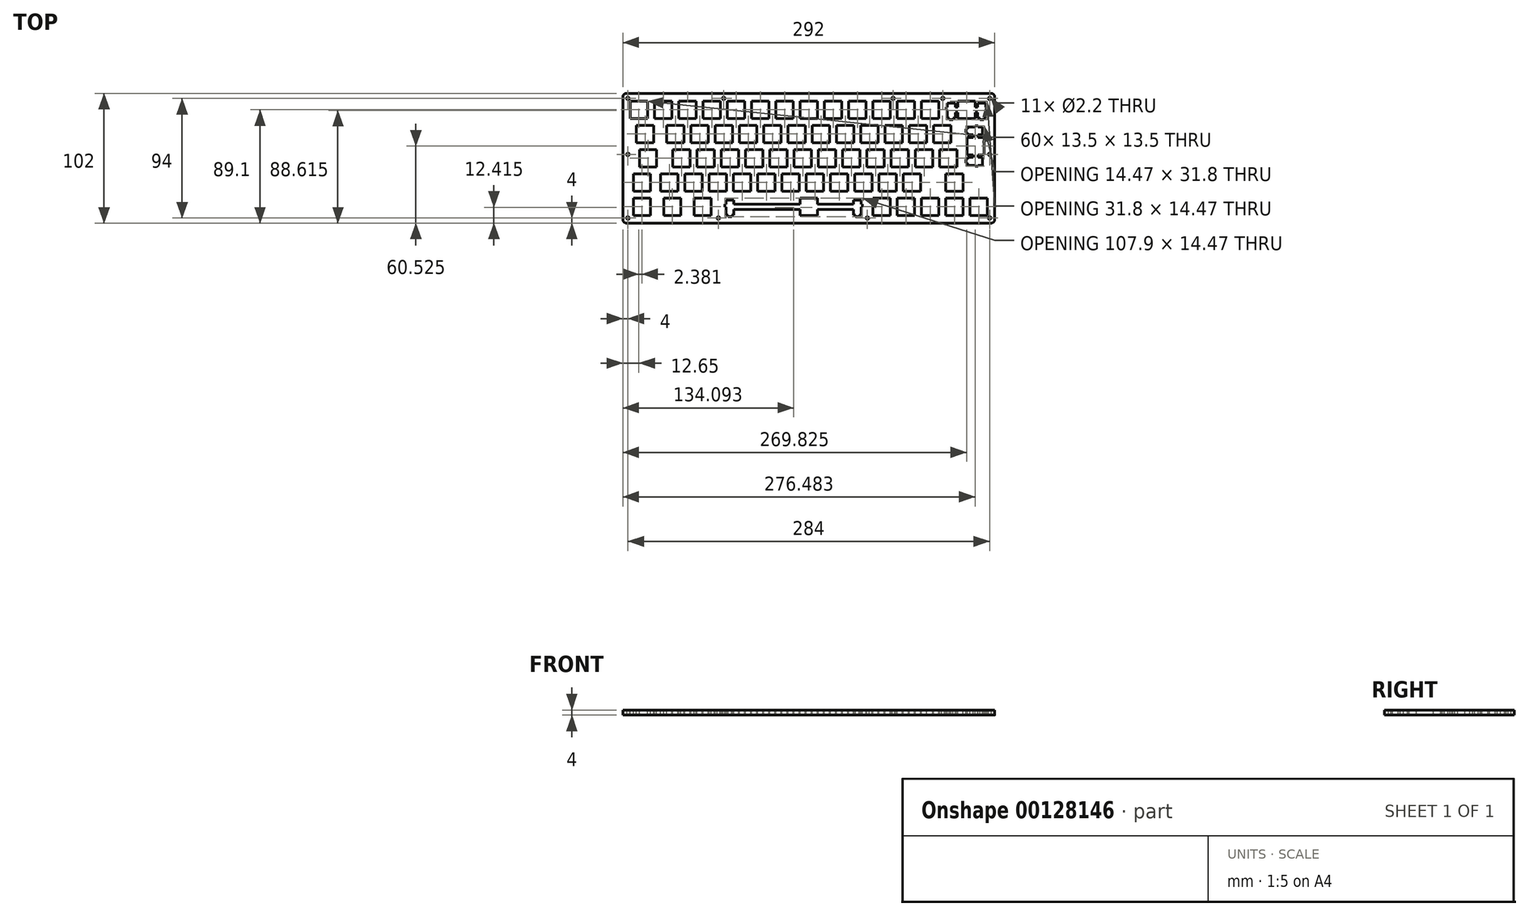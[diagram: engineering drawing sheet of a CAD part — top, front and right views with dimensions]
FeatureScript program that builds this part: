
annotation { "Feature Type Name" : "Feature", "Feature Type Description" : "" }
export const myFeature = defineFeature(function(context is Context, id is Id, definition is map)
    precondition{}
    {
        {
            var Q0;
            Q0=qCreatedBy(makeId("Top.planeOp"),FACE);
            var sketch = newSketch(context, id + "F0", { "sketchPlane" : qUnion([Q0])});
            skLineSegment(sketch, "E0.bottom", {"start": v(-143, 51) * mm, "end": v(143, 51) * mm});
            skLineSegment(sketch, "E0.top", {"start": v(-143, -51) * mm, "end": v(143, -51) * mm});
            skLineSegment(sketch, "E0.left", {"start": v(-146, 48) * mm, "end": v(-146, -48) * mm});
            skLineSegment(sketch, "E0.right", {"start": v(146, 48) * mm, "end": v(146, -48) * mm});
            skPoint(sketch, "E0.middle", {"position": v(0, 0) * mm});
            skPoint(sketch, "E1.visualSharp", {"position": v(-146, 51) * mm});
            skArc(sketch, "E1.filletArc", {"start": v(-143, 51) * mm, "mid": v(-145.12, 50.12) * mm, "end": v(-146, 48) * mm});
            skPoint(sketch, "E2.visualSharp", {"position": v(-146, -51) * mm});
            skArc(sketch, "E2.filletArc", {"start": v(-146, -48) * mm, "mid": v(-145.12, -50.12) * mm, "end": v(-143, -51) * mm});
            skPoint(sketch, "E3.visualSharp", {"position": v(146, 51) * mm});
            skArc(sketch, "E3.filletArc", {"start": v(146, 48) * mm, "mid": v(145.12, 50.12) * mm, "end": v(143, 51) * mm});
            skPoint(sketch, "E4.visualSharp", {"position": v(146, -51) * mm});
            skArc(sketch, "E4.filletArc", {"start": v(143, -51) * mm, "mid": v(145.12, -50.12) * mm, "end": v(146, -48) * mm});
            skCircle(sketch, "E5", {"center": v(-142, 47) * mm, "radius": 1.1 * mm});
            skCircle(sketch, "E6", {"center": v(-66.83, 47) * mm, "radius": 1.1 * mm});
            skCircle(sketch, "E7", {"center": v(66.17, 47) * mm, "radius": 1.1 * mm});
            skCircle(sketch, "E8", {"center": v(105.17, 47) * mm, "radius": 1.1 * mm});
            skCircle(sketch, "E9", {"center": v(142, 47) * mm, "radius": 1.1 * mm});
            skCircle(sketch, "E10", {"center": v(-142, -47) * mm, "radius": 1.1 * mm});
            skCircle(sketch, "E11", {"center": v(142, -47) * mm, "radius": 1.1 * mm});
            skCircle(sketch, "E12", {"center": v(-71, -47) * mm, "radius": 1.1 * mm});
            skCircle(sketch, "E13", {"center": v(46, -47) * mm, "radius": 1.1 * mm});
            skCircle(sketch, "E14", {"center": v(-142, 3) * mm, "radius": 1.1 * mm});
            skCircle(sketch, "E15", {"center": v(142, 3) * mm, "radius": 1.1 * mm});
            skSolve(sketch);
        }
        {
            var Q0;
            Q0=qSketchRegion(id+"F0",true);
            extrude(context, id + "F1", {"entities" : qUnion([Q0]), "depth" : 4 * mm});
        }
        {
            var Q0;
            Q0=makeQuery(id+"F1.opExtrude","CAP_FACE",FACE,{"disambiguationData":[OSD([sQuery(id+"F0.wireOp",EDGE,"E0.bottom"),sQuery(id+"F0.wireOp",EDGE,"E0.top"),sQuery(id+"F0.wireOp",EDGE,"E0.left"),sQuery(id+"F0.wireOp",EDGE,"E0.right"),sQuery(id+"F0.wireOp",EDGE,"E1.filletArc"),sQuery(id+"F0.wireOp",EDGE,"E2.filletArc"),sQuery(id+"F0.wireOp",EDGE,"E3.filletArc"),sQuery(id+"F0.wireOp",EDGE,"E4.filletArc"),sQuery(id+"F0.wireOp",EDGE,"E5"),sQuery(id+"F0.wireOp",EDGE,"E6"),sQuery(id+"F0.wireOp",EDGE,"E7"),sQuery(id+"F0.wireOp",EDGE,"E8"),sQuery(id+"F0.wireOp",EDGE,"E9"),sQuery(id+"F0.wireOp",EDGE,"E10"),sQuery(id+"F0.wireOp",EDGE,"E11"),sQuery(id+"F0.wireOp",EDGE,"E12"),sQuery(id+"F0.wireOp",EDGE,"E13"),sQuery(id+"F0.wireOp",EDGE,"E14"),sQuery(id+"F0.wireOp",EDGE,"E15")])],"isStart":false});
            var sketch = newSketch(context, id + "F2", { "sketchPlane" : qUnion([Q0])});
            skLineSegment(sketch, "E16", {"start": v(-18.66, -36.05) * mm, "end": v(-58.83, -36.05) * mm});
            skLineSegment(sketch, "E17", {"start": v(-58.83, -36.05) * mm, "end": v(-58.83, -32.82) * mm});
            skLineSegment(sketch, "E18", {"start": v(-58.83, -32.82) * mm, "end": v(-64.98, -32.82) * mm});
            skLineSegment(sketch, "E19", {"start": v(-64.98, -32.82) * mm, "end": v(-64.98, -36.05) * mm});
            skLineSegment(sketch, "E20", {"start": v(-64.98, -36.05) * mm, "end": v(-65.86, -36.05) * mm});
            skLineSegment(sketch, "E21", {"start": v(-65.86, -36.05) * mm, "end": v(-65.86, -38.35) * mm});
            skLineSegment(sketch, "E22", {"start": v(-65.86, -38.35) * mm, "end": v(-64.98, -38.35) * mm});
            skLineSegment(sketch, "E23", {"start": v(-64.98, -38.35) * mm, "end": v(-64.98, -44.62) * mm});
            skLineSegment(sketch, "E24", {"start": v(-64.98, -44.62) * mm, "end": v(-63.3, -44.62) * mm});
            skLineSegment(sketch, "E25", {"start": v(-63.3, -44.62) * mm, "end": v(-63.3, -45.82) * mm});
            skLineSegment(sketch, "E26", {"start": v(-63.3, -45.82) * mm, "end": v(-60.5, -45.82) * mm});
            skLineSegment(sketch, "E27", {"start": v(-60.5, -45.82) * mm, "end": v(-60.5, -44.62) * mm});
            skLineSegment(sketch, "E28", {"start": v(-60.5, -44.62) * mm, "end": v(-58.83, -44.62) * mm});
            skLineSegment(sketch, "E29", {"start": v(-58.83, -44.62) * mm, "end": v(-58.83, -40.15) * mm});
            skLineSegment(sketch, "E30", {"start": v(-58.83, -40.15) * mm, "end": v(-18.66, -40.15) * mm});
            skLineSegment(sketch, "E31", {"start": v(-6.75, -44.85) * mm, "end": v(-5.16, -44.85) * mm});
            skLineSegment(sketch, "E32", {"start": v(6.75, -40.15) * mm, "end": v(35.02, -40.15) * mm});
            skLineSegment(sketch, "E33", {"start": v(35.02, -40.15) * mm, "end": v(35.02, -44.62) * mm});
            skLineSegment(sketch, "E34", {"start": v(35.02, -44.62) * mm, "end": v(36.7, -44.62) * mm});
            skLineSegment(sketch, "E35", {"start": v(36.7, -44.62) * mm, "end": v(36.7, -45.82) * mm});
            skLineSegment(sketch, "E36", {"start": v(36.7, -45.82) * mm, "end": v(39.5, -45.82) * mm});
            skLineSegment(sketch, "E37", {"start": v(39.5, -45.82) * mm, "end": v(39.5, -44.62) * mm});
            skLineSegment(sketch, "E38", {"start": v(39.5, -44.62) * mm, "end": v(41.17, -44.62) * mm});
            skLineSegment(sketch, "E39", {"start": v(41.17, -44.62) * mm, "end": v(41.17, -38.35) * mm});
            skLineSegment(sketch, "E40", {"start": v(41.17, -38.35) * mm, "end": v(42.04, -38.35) * mm});
            skLineSegment(sketch, "E41", {"start": v(42.04, -38.35) * mm, "end": v(42.04, -36.05) * mm});
            skLineSegment(sketch, "E42", {"start": v(42.04, -36.05) * mm, "end": v(41.17, -36.05) * mm});
            skLineSegment(sketch, "E43", {"start": v(41.17, -36.05) * mm, "end": v(41.17, -32.82) * mm});
            skLineSegment(sketch, "E44", {"start": v(41.17, -32.82) * mm, "end": v(35.02, -32.82) * mm});
            skLineSegment(sketch, "E45", {"start": v(35.02, -32.82) * mm, "end": v(35.02, -36.05) * mm});
            skLineSegment(sketch, "E46", {"start": v(35.02, -36.05) * mm, "end": v(6.75, -36.05) * mm});
            skLineSegment(sketch, "E47", {"start": v(-137.72, -31.35) * mm, "end": v(-124.22, -31.35) * mm});
            skLineSegment(sketch, "E48", {"start": v(-124.22, -31.35) * mm, "end": v(-124.22, -44.85) * mm});
            skLineSegment(sketch, "E49", {"start": v(-124.22, -44.85) * mm, "end": v(-137.72, -44.85) * mm});
            skLineSegment(sketch, "E50", {"start": v(-137.72, -44.85) * mm, "end": v(-137.72, -31.35) * mm});
            skLineSegment(sketch, "E51", {"start": v(-113.9, -31.35) * mm, "end": v(-100.4, -31.35) * mm});
            skLineSegment(sketch, "E52", {"start": v(-100.4, -31.35) * mm, "end": v(-100.4, -44.85) * mm});
            skLineSegment(sketch, "E53", {"start": v(-100.4, -44.85) * mm, "end": v(-113.9, -44.85) * mm});
            skLineSegment(sketch, "E54", {"start": v(-113.9, -44.85) * mm, "end": v(-113.9, -31.35) * mm});
            skLineSegment(sketch, "E55", {"start": v(-90.1, -31.35) * mm, "end": v(-76.6, -31.35) * mm});
            skLineSegment(sketch, "E56", {"start": v(-76.6, -31.35) * mm, "end": v(-76.6, -44.85) * mm});
            skLineSegment(sketch, "E57", {"start": v(-76.6, -44.85) * mm, "end": v(-90.1, -44.85) * mm});
            skLineSegment(sketch, "E58", {"start": v(-90.1, -44.85) * mm, "end": v(-90.1, -31.35) * mm});
            skLineSegment(sketch, "E59", {"start": v(50.4, -31.35) * mm, "end": v(63.9, -31.35) * mm});
            skLineSegment(sketch, "E60", {"start": v(63.9, -31.35) * mm, "end": v(63.9, -44.85) * mm});
            skLineSegment(sketch, "E61", {"start": v(63.9, -44.85) * mm, "end": v(50.4, -44.85) * mm});
            skLineSegment(sketch, "E62", {"start": v(50.4, -44.85) * mm, "end": v(50.4, -31.35) * mm});
            skLineSegment(sketch, "E63", {"start": v(69.45, -31.35) * mm, "end": v(82.95, -31.35) * mm});
            skLineSegment(sketch, "E64", {"start": v(82.95, -31.35) * mm, "end": v(82.95, -44.85) * mm});
            skLineSegment(sketch, "E65", {"start": v(82.95, -44.85) * mm, "end": v(69.45, -44.85) * mm});
            skLineSegment(sketch, "E66", {"start": v(69.45, -44.85) * mm, "end": v(69.45, -31.35) * mm});
            skLineSegment(sketch, "E67", {"start": v(88.5, -31.35) * mm, "end": v(102, -31.35) * mm});
            skLineSegment(sketch, "E68", {"start": v(102, -31.35) * mm, "end": v(102, -44.85) * mm});
            skLineSegment(sketch, "E69", {"start": v(102, -44.85) * mm, "end": v(88.5, -44.85) * mm});
            skLineSegment(sketch, "E70", {"start": v(88.5, -44.85) * mm, "end": v(88.5, -31.35) * mm});
            skLineSegment(sketch, "E71", {"start": v(107.55, -31.35) * mm, "end": v(121.05, -31.35) * mm});
            skLineSegment(sketch, "E72", {"start": v(121.05, -31.35) * mm, "end": v(121.05, -44.85) * mm});
            skLineSegment(sketch, "E73", {"start": v(121.05, -44.85) * mm, "end": v(107.55, -44.85) * mm});
            skLineSegment(sketch, "E74", {"start": v(107.55, -44.85) * mm, "end": v(107.55, -31.35) * mm});
            skLineSegment(sketch, "E75", {"start": v(126.6, -31.35) * mm, "end": v(140.1, -31.35) * mm});
            skLineSegment(sketch, "E76", {"start": v(140.1, -31.35) * mm, "end": v(140.1, -44.85) * mm});
            skLineSegment(sketch, "E77", {"start": v(140.1, -44.85) * mm, "end": v(126.6, -44.85) * mm});
            skLineSegment(sketch, "E78", {"start": v(126.6, -44.85) * mm, "end": v(126.6, -31.35) * mm});
            skLineSegment(sketch, "E79", {"start": v(-137.72, -12.3) * mm, "end": v(-124.22, -12.3) * mm});
            skLineSegment(sketch, "E80", {"start": v(-124.22, -12.3) * mm, "end": v(-124.22, -25.8) * mm});
            skLineSegment(sketch, "E81", {"start": v(-124.22, -25.8) * mm, "end": v(-137.72, -25.8) * mm});
            skLineSegment(sketch, "E82", {"start": v(-137.72, -25.8) * mm, "end": v(-137.72, -12.3) * mm});
            skLineSegment(sketch, "E83", {"start": v(-116.29, -12.3) * mm, "end": v(-102.79, -12.3) * mm});
            skLineSegment(sketch, "E84", {"start": v(-102.79, -12.3) * mm, "end": v(-102.79, -25.8) * mm});
            skLineSegment(sketch, "E85", {"start": v(-102.79, -25.8) * mm, "end": v(-116.29, -25.8) * mm});
            skLineSegment(sketch, "E86", {"start": v(-116.29, -25.8) * mm, "end": v(-116.29, -12.3) * mm});
            skLineSegment(sketch, "E87", {"start": v(-97.24, -12.3) * mm, "end": v(-83.74, -12.3) * mm});
            skLineSegment(sketch, "E88", {"start": v(-83.74, -12.3) * mm, "end": v(-83.74, -25.8) * mm});
            skLineSegment(sketch, "E89", {"start": v(-83.74, -25.8) * mm, "end": v(-97.24, -25.8) * mm});
            skLineSegment(sketch, "E90", {"start": v(-97.24, -25.8) * mm, "end": v(-97.24, -12.3) * mm});
            skLineSegment(sketch, "E91", {"start": v(-78.19, -12.3) * mm, "end": v(-64.69, -12.3) * mm});
            skLineSegment(sketch, "E92", {"start": v(-64.69, -12.3) * mm, "end": v(-64.69, -25.8) * mm});
            skLineSegment(sketch, "E93", {"start": v(-64.69, -25.8) * mm, "end": v(-78.19, -25.8) * mm});
            skLineSegment(sketch, "E94", {"start": v(-78.19, -25.8) * mm, "end": v(-78.19, -12.3) * mm});
            skLineSegment(sketch, "E95", {"start": v(-59.14, -12.3) * mm, "end": v(-45.64, -12.3) * mm});
            skLineSegment(sketch, "E96", {"start": v(-45.64, -12.3) * mm, "end": v(-45.64, -25.8) * mm});
            skLineSegment(sketch, "E97", {"start": v(-45.64, -25.8) * mm, "end": v(-59.14, -25.8) * mm});
            skLineSegment(sketch, "E98", {"start": v(-59.14, -25.8) * mm, "end": v(-59.14, -12.3) * mm});
            skLineSegment(sketch, "E99", {"start": v(-40.09, -12.3) * mm, "end": v(-26.59, -12.3) * mm});
            skLineSegment(sketch, "E100", {"start": v(-26.59, -12.3) * mm, "end": v(-26.59, -25.8) * mm});
            skLineSegment(sketch, "E101", {"start": v(-26.59, -25.8) * mm, "end": v(-40.09, -25.8) * mm});
            skLineSegment(sketch, "E102", {"start": v(-40.09, -25.8) * mm, "end": v(-40.09, -12.3) * mm});
            skLineSegment(sketch, "E103", {"start": v(-21.04, -12.3) * mm, "end": v(-7.54, -12.3) * mm});
            skLineSegment(sketch, "E104", {"start": v(-7.54, -12.3) * mm, "end": v(-7.54, -25.8) * mm});
            skLineSegment(sketch, "E105", {"start": v(-7.54, -25.8) * mm, "end": v(-21.04, -25.8) * mm});
            skLineSegment(sketch, "E106", {"start": v(-21.04, -25.8) * mm, "end": v(-21.04, -12.3) * mm});
            skLineSegment(sketch, "E107", {"start": v(-1.99, -12.3) * mm, "end": v(11.51, -12.3) * mm});
            skLineSegment(sketch, "E108", {"start": v(11.51, -12.3) * mm, "end": v(11.51, -25.8) * mm});
            skLineSegment(sketch, "E109", {"start": v(11.51, -25.8) * mm, "end": v(-1.99, -25.8) * mm});
            skLineSegment(sketch, "E110", {"start": v(-1.99, -25.8) * mm, "end": v(-1.99, -12.3) * mm});
            skLineSegment(sketch, "E111", {"start": v(17.06, -12.3) * mm, "end": v(30.56, -12.3) * mm});
            skLineSegment(sketch, "E112", {"start": v(30.56, -12.3) * mm, "end": v(30.56, -25.8) * mm});
            skLineSegment(sketch, "E113", {"start": v(30.56, -25.8) * mm, "end": v(17.06, -25.8) * mm});
            skLineSegment(sketch, "E114", {"start": v(17.06, -25.8) * mm, "end": v(17.06, -12.3) * mm});
            skLineSegment(sketch, "E115", {"start": v(36.11, -12.3) * mm, "end": v(49.61, -12.3) * mm});
            skLineSegment(sketch, "E116", {"start": v(49.61, -12.3) * mm, "end": v(49.61, -25.8) * mm});
            skLineSegment(sketch, "E117", {"start": v(49.61, -25.8) * mm, "end": v(36.11, -25.8) * mm});
            skLineSegment(sketch, "E118", {"start": v(36.11, -25.8) * mm, "end": v(36.11, -12.3) * mm});
            skLineSegment(sketch, "E119", {"start": v(55.16, -12.3) * mm, "end": v(68.66, -12.3) * mm});
            skLineSegment(sketch, "E120", {"start": v(68.66, -12.3) * mm, "end": v(68.66, -25.8) * mm});
            skLineSegment(sketch, "E121", {"start": v(68.66, -25.8) * mm, "end": v(55.16, -25.8) * mm});
            skLineSegment(sketch, "E122", {"start": v(55.16, -25.8) * mm, "end": v(55.16, -12.3) * mm});
            skLineSegment(sketch, "E123", {"start": v(74.21, -12.3) * mm, "end": v(87.71, -12.3) * mm});
            skLineSegment(sketch, "E124", {"start": v(87.71, -12.3) * mm, "end": v(87.71, -25.8) * mm});
            skLineSegment(sketch, "E125", {"start": v(87.71, -25.8) * mm, "end": v(74.21, -25.8) * mm});
            skLineSegment(sketch, "E126", {"start": v(74.21, -25.8) * mm, "end": v(74.21, -12.3) * mm});
            skLineSegment(sketch, "E127", {"start": v(107.55, -12.3) * mm, "end": v(121.05, -12.3) * mm});
            skLineSegment(sketch, "E128", {"start": v(121.05, -12.3) * mm, "end": v(121.05, -25.8) * mm});
            skLineSegment(sketch, "E129", {"start": v(121.05, -25.8) * mm, "end": v(107.55, -25.8) * mm});
            skLineSegment(sketch, "E130", {"start": v(107.55, -25.8) * mm, "end": v(107.55, -12.3) * mm});
            skLineSegment(sketch, "E131", {"start": v(-132.96, 6.75) * mm, "end": v(-119.46, 6.75) * mm});
            skLineSegment(sketch, "E132", {"start": v(-119.46, 6.75) * mm, "end": v(-119.46, -6.75) * mm});
            skLineSegment(sketch, "E133", {"start": v(-119.46, -6.75) * mm, "end": v(-132.96, -6.75) * mm});
            skLineSegment(sketch, "E134", {"start": v(-132.96, -6.75) * mm, "end": v(-132.96, 6.75) * mm});
            skLineSegment(sketch, "E135", {"start": v(-106.76, 6.75) * mm, "end": v(-93.26, 6.75) * mm});
            skLineSegment(sketch, "E136", {"start": v(-93.26, 6.75) * mm, "end": v(-93.26, -6.75) * mm});
            skLineSegment(sketch, "E137", {"start": v(-93.26, -6.75) * mm, "end": v(-106.76, -6.75) * mm});
            skLineSegment(sketch, "E138", {"start": v(-106.76, -6.75) * mm, "end": v(-106.76, 6.75) * mm});
            skLineSegment(sketch, "E139", {"start": v(-87.71, 6.75) * mm, "end": v(-74.21, 6.75) * mm});
            skLineSegment(sketch, "E140", {"start": v(-74.21, 6.75) * mm, "end": v(-74.21, -6.75) * mm});
            skLineSegment(sketch, "E141", {"start": v(-74.21, -6.75) * mm, "end": v(-87.71, -6.75) * mm});
            skLineSegment(sketch, "E142", {"start": v(-87.71, -6.75) * mm, "end": v(-87.71, 6.75) * mm});
            skLineSegment(sketch, "E143", {"start": v(-68.66, 6.75) * mm, "end": v(-55.16, 6.75) * mm});
            skLineSegment(sketch, "E144", {"start": v(-55.16, 6.75) * mm, "end": v(-55.16, -6.75) * mm});
            skLineSegment(sketch, "E145", {"start": v(-55.16, -6.75) * mm, "end": v(-68.66, -6.75) * mm});
            skLineSegment(sketch, "E146", {"start": v(-68.66, -6.75) * mm, "end": v(-68.66, 6.75) * mm});
            skLineSegment(sketch, "E147", {"start": v(-49.61, 6.75) * mm, "end": v(-36.11, 6.75) * mm});
            skLineSegment(sketch, "E148", {"start": v(-36.11, 6.75) * mm, "end": v(-36.11, -6.75) * mm});
            skLineSegment(sketch, "E149", {"start": v(-36.11, -6.75) * mm, "end": v(-49.61, -6.75) * mm});
            skLineSegment(sketch, "E150", {"start": v(-49.61, -6.75) * mm, "end": v(-49.61, 6.75) * mm});
            skLineSegment(sketch, "E151", {"start": v(-30.56, 6.75) * mm, "end": v(-17.06, 6.75) * mm});
            skLineSegment(sketch, "E152", {"start": v(-17.06, 6.75) * mm, "end": v(-17.06, -6.75) * mm});
            skLineSegment(sketch, "E153", {"start": v(-17.06, -6.75) * mm, "end": v(-30.56, -6.75) * mm});
            skLineSegment(sketch, "E154", {"start": v(-30.56, -6.75) * mm, "end": v(-30.56, 6.75) * mm});
            skLineSegment(sketch, "E155", {"start": v(-11.51, 6.75) * mm, "end": v(1.99, 6.75) * mm});
            skLineSegment(sketch, "E156", {"start": v(1.99, 6.75) * mm, "end": v(1.99, -6.75) * mm});
            skLineSegment(sketch, "E157", {"start": v(1.99, -6.75) * mm, "end": v(-11.51, -6.75) * mm});
            skLineSegment(sketch, "E158", {"start": v(-11.51, -6.75) * mm, "end": v(-11.51, 6.75) * mm});
            skLineSegment(sketch, "E159", {"start": v(7.54, 6.75) * mm, "end": v(21.04, 6.75) * mm});
            skLineSegment(sketch, "E160", {"start": v(21.04, 6.75) * mm, "end": v(21.04, -6.75) * mm});
            skLineSegment(sketch, "E161", {"start": v(21.04, -6.75) * mm, "end": v(7.54, -6.75) * mm});
            skLineSegment(sketch, "E162", {"start": v(7.54, -6.75) * mm, "end": v(7.54, 6.75) * mm});
            skLineSegment(sketch, "E163", {"start": v(26.59, 6.75) * mm, "end": v(40.09, 6.75) * mm});
            skLineSegment(sketch, "E164", {"start": v(40.09, 6.75) * mm, "end": v(40.09, -6.75) * mm});
            skLineSegment(sketch, "E165", {"start": v(40.09, -6.75) * mm, "end": v(26.59, -6.75) * mm});
            skLineSegment(sketch, "E166", {"start": v(26.59, -6.75) * mm, "end": v(26.59, 6.75) * mm});
            skLineSegment(sketch, "E167", {"start": v(45.64, 6.75) * mm, "end": v(59.14, 6.75) * mm});
            skLineSegment(sketch, "E168", {"start": v(59.14, 6.75) * mm, "end": v(59.14, -6.75) * mm});
            skLineSegment(sketch, "E169", {"start": v(59.14, -6.75) * mm, "end": v(45.64, -6.75) * mm});
            skLineSegment(sketch, "E170", {"start": v(45.64, -6.75) * mm, "end": v(45.64, 6.75) * mm});
            skLineSegment(sketch, "E171", {"start": v(64.69, 6.75) * mm, "end": v(78.19, 6.75) * mm});
            skLineSegment(sketch, "E172", {"start": v(78.19, 6.75) * mm, "end": v(78.19, -6.75) * mm});
            skLineSegment(sketch, "E173", {"start": v(78.19, -6.75) * mm, "end": v(64.69, -6.75) * mm});
            skLineSegment(sketch, "E174", {"start": v(64.69, -6.75) * mm, "end": v(64.69, 6.75) * mm});
            skLineSegment(sketch, "E175", {"start": v(83.74, 6.75) * mm, "end": v(97.24, 6.75) * mm});
            skLineSegment(sketch, "E176", {"start": v(97.24, 6.75) * mm, "end": v(97.24, -6.75) * mm});
            skLineSegment(sketch, "E177", {"start": v(97.24, -6.75) * mm, "end": v(83.74, -6.75) * mm});
            skLineSegment(sketch, "E178", {"start": v(83.74, -6.75) * mm, "end": v(83.74, 6.75) * mm});
            skLineSegment(sketch, "E179", {"start": v(102.79, 6.75) * mm, "end": v(116.29, 6.75) * mm});
            skLineSegment(sketch, "E180", {"start": v(116.29, 6.75) * mm, "end": v(116.29, -6.75) * mm});
            skLineSegment(sketch, "E181", {"start": v(116.29, -6.75) * mm, "end": v(102.79, -6.75) * mm});
            skLineSegment(sketch, "E182", {"start": v(102.79, -6.75) * mm, "end": v(102.79, 6.75) * mm});
            skLineSegment(sketch, "E183", {"start": v(130.72, 25.43) * mm, "end": v(130.72, 24.55) * mm});
            skLineSegment(sketch, "E184", {"start": v(130.72, 24.55) * mm, "end": v(124.45, 24.55) * mm});
            skLineSegment(sketch, "E185", {"start": v(124.45, 24.55) * mm, "end": v(124.45, 22.87) * mm});
            skLineSegment(sketch, "E186", {"start": v(124.45, 22.87) * mm, "end": v(123.25, 22.87) * mm});
            skLineSegment(sketch, "E187", {"start": v(123.25, 22.87) * mm, "end": v(123.25, 20.07) * mm});
            skLineSegment(sketch, "E188", {"start": v(123.25, 20.07) * mm, "end": v(124.45, 20.07) * mm});
            skLineSegment(sketch, "E189", {"start": v(124.45, 20.07) * mm, "end": v(124.45, 18.4) * mm});
            skLineSegment(sketch, "E190", {"start": v(124.45, 18.4) * mm, "end": v(128.92, 18.4) * mm});
            skLineSegment(sketch, "E191", {"start": v(128.92, 18.4) * mm, "end": v(128.92, 16.28) * mm});
            skLineSegment(sketch, "E192", {"start": v(128.92, 16.28) * mm, "end": v(124.22, 16.28) * mm});
            skLineSegment(sketch, "E193", {"start": v(124.22, 16.28) * mm, "end": v(124.22, 2.77) * mm});
            skLineSegment(sketch, "E194", {"start": v(124.22, 2.77) * mm, "end": v(128.92, 2.77) * mm});
            skLineSegment(sketch, "E195", {"start": v(128.92, 2.77) * mm, "end": v(128.92, 0.65) * mm});
            skLineSegment(sketch, "E196", {"start": v(128.92, 0.65) * mm, "end": v(124.45, 0.65) * mm});
            skLineSegment(sketch, "E197", {"start": v(124.45, 0.65) * mm, "end": v(124.45, -1.02) * mm});
            skLineSegment(sketch, "E198", {"start": v(124.45, -1.02) * mm, "end": v(123.25, -1.02) * mm});
            skLineSegment(sketch, "E199", {"start": v(123.25, -1.02) * mm, "end": v(123.25, -3.82) * mm});
            skLineSegment(sketch, "E200", {"start": v(123.25, -3.82) * mm, "end": v(124.45, -3.82) * mm});
            skLineSegment(sketch, "E201", {"start": v(124.45, -3.82) * mm, "end": v(124.45, -5.5) * mm});
            skLineSegment(sketch, "E202", {"start": v(124.45, -5.5) * mm, "end": v(130.72, -5.5) * mm});
            skLineSegment(sketch, "E203", {"start": v(130.72, -5.5) * mm, "end": v(130.72, -6.38) * mm});
            skLineSegment(sketch, "E204", {"start": v(130.72, -6.38) * mm, "end": v(133.02, -6.38) * mm});
            skLineSegment(sketch, "E205", {"start": v(133.02, -6.38) * mm, "end": v(133.02, -5.5) * mm});
            skLineSegment(sketch, "E206", {"start": v(133.02, -5.5) * mm, "end": v(136.25, -5.5) * mm});
            skLineSegment(sketch, "E207", {"start": v(136.25, -5.5) * mm, "end": v(136.25, 0.65) * mm});
            skLineSegment(sketch, "E208", {"start": v(136.25, 0.65) * mm, "end": v(133.02, 0.65) * mm});
            skLineSegment(sketch, "E209", {"start": v(133.02, 0.65) * mm, "end": v(133.02, 2.77) * mm});
            skLineSegment(sketch, "E210", {"start": v(133.02, 2.77) * mm, "end": v(137.72, 2.77) * mm});
            skLineSegment(sketch, "E211", {"start": v(137.72, 2.77) * mm, "end": v(137.72, 16.28) * mm});
            skLineSegment(sketch, "E212", {"start": v(137.72, 16.28) * mm, "end": v(133.02, 16.28) * mm});
            skLineSegment(sketch, "E213", {"start": v(133.02, 16.28) * mm, "end": v(133.02, 18.4) * mm});
            skLineSegment(sketch, "E214", {"start": v(133.02, 18.4) * mm, "end": v(136.25, 18.4) * mm});
            skLineSegment(sketch, "E215", {"start": v(136.25, 18.4) * mm, "end": v(136.25, 24.55) * mm});
            skLineSegment(sketch, "E216", {"start": v(136.25, 24.55) * mm, "end": v(133.02, 24.55) * mm});
            skLineSegment(sketch, "E217", {"start": v(133.02, 24.55) * mm, "end": v(133.02, 25.43) * mm});
            skLineSegment(sketch, "E218", {"start": v(133.02, 25.43) * mm, "end": v(130.72, 25.43) * mm});
            skLineSegment(sketch, "E219", {"start": v(-135.34, 25.8) * mm, "end": v(-121.84, 25.8) * mm});
            skLineSegment(sketch, "E220", {"start": v(-121.84, 25.8) * mm, "end": v(-121.84, 12.3) * mm});
            skLineSegment(sketch, "E221", {"start": v(-121.84, 12.3) * mm, "end": v(-135.34, 12.3) * mm});
            skLineSegment(sketch, "E222", {"start": v(-135.34, 12.3) * mm, "end": v(-135.34, 25.8) * mm});
            skLineSegment(sketch, "E223", {"start": v(-111.53, 25.8) * mm, "end": v(-98.02, 25.8) * mm});
            skLineSegment(sketch, "E224", {"start": v(-98.02, 25.8) * mm, "end": v(-98.02, 12.3) * mm});
            skLineSegment(sketch, "E225", {"start": v(-98.02, 12.3) * mm, "end": v(-111.53, 12.3) * mm});
            skLineSegment(sketch, "E226", {"start": v(-111.53, 12.3) * mm, "end": v(-111.53, 25.8) * mm});
            skLineSegment(sketch, "E227", {"start": v(-92.48, 25.8) * mm, "end": v(-78.97, 25.8) * mm});
            skLineSegment(sketch, "E228", {"start": v(-78.97, 25.8) * mm, "end": v(-78.97, 12.3) * mm});
            skLineSegment(sketch, "E229", {"start": v(-78.97, 12.3) * mm, "end": v(-92.48, 12.3) * mm});
            skLineSegment(sketch, "E230", {"start": v(-92.48, 12.3) * mm, "end": v(-92.48, 25.8) * mm});
            skLineSegment(sketch, "E231", {"start": v(-73.43, 25.8) * mm, "end": v(-59.92, 25.8) * mm});
            skLineSegment(sketch, "E232", {"start": v(-59.92, 25.8) * mm, "end": v(-59.92, 12.3) * mm});
            skLineSegment(sketch, "E233", {"start": v(-59.92, 12.3) * mm, "end": v(-73.43, 12.3) * mm});
            skLineSegment(sketch, "E234", {"start": v(-73.43, 12.3) * mm, "end": v(-73.43, 25.8) * mm});
            skLineSegment(sketch, "E235", {"start": v(-54.38, 25.8) * mm, "end": v(-40.87, 25.8) * mm});
            skLineSegment(sketch, "E236", {"start": v(-40.87, 25.8) * mm, "end": v(-40.87, 12.3) * mm});
            skLineSegment(sketch, "E237", {"start": v(-40.87, 12.3) * mm, "end": v(-54.38, 12.3) * mm});
            skLineSegment(sketch, "E238", {"start": v(-54.38, 12.3) * mm, "end": v(-54.38, 25.8) * mm});
            skLineSegment(sketch, "E239", {"start": v(-35.32, 25.8) * mm, "end": v(-21.82, 25.8) * mm});
            skLineSegment(sketch, "E240", {"start": v(-21.82, 25.8) * mm, "end": v(-21.82, 12.3) * mm});
            skLineSegment(sketch, "E241", {"start": v(-21.82, 12.3) * mm, "end": v(-35.32, 12.3) * mm});
            skLineSegment(sketch, "E242", {"start": v(-35.32, 12.3) * mm, "end": v(-35.32, 25.8) * mm});
            skLineSegment(sketch, "E243", {"start": v(-16.27, 25.8) * mm, "end": v(-2.77, 25.8) * mm});
            skLineSegment(sketch, "E244", {"start": v(-2.77, 25.8) * mm, "end": v(-2.77, 12.3) * mm});
            skLineSegment(sketch, "E245", {"start": v(-2.77, 12.3) * mm, "end": v(-16.27, 12.3) * mm});
            skLineSegment(sketch, "E246", {"start": v(-16.27, 12.3) * mm, "end": v(-16.27, 25.8) * mm});
            skLineSegment(sketch, "E247", {"start": v(2.78, 25.8) * mm, "end": v(16.28, 25.8) * mm});
            skLineSegment(sketch, "E248", {"start": v(16.28, 25.8) * mm, "end": v(16.28, 12.3) * mm});
            skLineSegment(sketch, "E249", {"start": v(16.28, 12.3) * mm, "end": v(2.78, 12.3) * mm});
            skLineSegment(sketch, "E250", {"start": v(2.78, 12.3) * mm, "end": v(2.78, 25.8) * mm});
            skLineSegment(sketch, "E251", {"start": v(21.83, 25.8) * mm, "end": v(35.33, 25.8) * mm});
            skLineSegment(sketch, "E252", {"start": v(35.33, 25.8) * mm, "end": v(35.33, 12.3) * mm});
            skLineSegment(sketch, "E253", {"start": v(35.33, 12.3) * mm, "end": v(21.83, 12.3) * mm});
            skLineSegment(sketch, "E254", {"start": v(21.83, 12.3) * mm, "end": v(21.83, 25.8) * mm});
            skLineSegment(sketch, "E255", {"start": v(40.88, 25.8) * mm, "end": v(54.38, 25.8) * mm});
            skLineSegment(sketch, "E256", {"start": v(54.38, 25.8) * mm, "end": v(54.38, 12.3) * mm});
            skLineSegment(sketch, "E257", {"start": v(54.38, 12.3) * mm, "end": v(40.88, 12.3) * mm});
            skLineSegment(sketch, "E258", {"start": v(40.88, 12.3) * mm, "end": v(40.88, 25.8) * mm});
            skLineSegment(sketch, "E259", {"start": v(59.93, 25.8) * mm, "end": v(73.43, 25.8) * mm});
            skLineSegment(sketch, "E260", {"start": v(73.43, 25.8) * mm, "end": v(73.43, 12.3) * mm});
            skLineSegment(sketch, "E261", {"start": v(73.43, 12.3) * mm, "end": v(59.93, 12.3) * mm});
            skLineSegment(sketch, "E262", {"start": v(59.93, 12.3) * mm, "end": v(59.93, 25.8) * mm});
            skLineSegment(sketch, "E263", {"start": v(78.98, 25.8) * mm, "end": v(92.48, 25.8) * mm});
            skLineSegment(sketch, "E264", {"start": v(92.48, 25.8) * mm, "end": v(92.48, 12.3) * mm});
            skLineSegment(sketch, "E265", {"start": v(92.48, 12.3) * mm, "end": v(78.98, 12.3) * mm});
            skLineSegment(sketch, "E266", {"start": v(78.98, 12.3) * mm, "end": v(78.98, 25.8) * mm});
            skLineSegment(sketch, "E267", {"start": v(98.03, 25.8) * mm, "end": v(111.52, 25.8) * mm});
            skLineSegment(sketch, "E268", {"start": v(111.52, 25.8) * mm, "end": v(111.52, 12.3) * mm});
            skLineSegment(sketch, "E269", {"start": v(111.52, 12.3) * mm, "end": v(98.03, 12.3) * mm});
            skLineSegment(sketch, "E270", {"start": v(98.03, 12.3) * mm, "end": v(98.03, 25.8) * mm});
            skLineSegment(sketch, "E271", {"start": v(117.08, 44.85) * mm, "end": v(117.08, 40.15) * mm});
            skLineSegment(sketch, "E272", {"start": v(117.08, 40.15) * mm, "end": v(114.95, 40.15) * mm});
            skLineSegment(sketch, "E273", {"start": v(114.95, 40.15) * mm, "end": v(114.95, 43.38) * mm});
            skLineSegment(sketch, "E274", {"start": v(114.95, 43.38) * mm, "end": v(108.8, 43.38) * mm});
            skLineSegment(sketch, "E275", {"start": v(108.8, 43.38) * mm, "end": v(108.8, 40.15) * mm});
            skLineSegment(sketch, "E276", {"start": v(108.8, 40.15) * mm, "end": v(107.92, 40.15) * mm});
            skLineSegment(sketch, "E277", {"start": v(107.92, 40.15) * mm, "end": v(107.92, 37.85) * mm});
            skLineSegment(sketch, "E278", {"start": v(107.92, 37.85) * mm, "end": v(108.8, 37.85) * mm});
            skLineSegment(sketch, "E279", {"start": v(108.8, 37.85) * mm, "end": v(108.8, 31.58) * mm});
            skLineSegment(sketch, "E280", {"start": v(108.8, 31.58) * mm, "end": v(110.48, 31.58) * mm});
            skLineSegment(sketch, "E281", {"start": v(110.48, 31.58) * mm, "end": v(110.48, 30.38) * mm});
            skLineSegment(sketch, "E282", {"start": v(110.48, 30.38) * mm, "end": v(113.27, 30.38) * mm});
            skLineSegment(sketch, "E283", {"start": v(113.27, 30.38) * mm, "end": v(113.27, 31.58) * mm});
            skLineSegment(sketch, "E284", {"start": v(113.27, 31.58) * mm, "end": v(114.95, 31.58) * mm});
            skLineSegment(sketch, "E285", {"start": v(114.95, 31.58) * mm, "end": v(114.95, 36.05) * mm});
            skLineSegment(sketch, "E286", {"start": v(114.95, 36.05) * mm, "end": v(117.08, 36.05) * mm});
            skLineSegment(sketch, "E287", {"start": v(117.08, 36.05) * mm, "end": v(117.08, 31.35) * mm});
            skLineSegment(sketch, "E288", {"start": v(117.08, 31.35) * mm, "end": v(130.58, 31.35) * mm});
            skLineSegment(sketch, "E289", {"start": v(130.58, 31.35) * mm, "end": v(130.58, 36.05) * mm});
            skLineSegment(sketch, "E290", {"start": v(130.58, 36.05) * mm, "end": v(132.7, 36.05) * mm});
            skLineSegment(sketch, "E291", {"start": v(132.7, 36.05) * mm, "end": v(132.7, 31.58) * mm});
            skLineSegment(sketch, "E292", {"start": v(132.7, 31.58) * mm, "end": v(134.37, 31.58) * mm});
            skLineSegment(sketch, "E293", {"start": v(134.37, 31.58) * mm, "end": v(134.37, 30.38) * mm});
            skLineSegment(sketch, "E294", {"start": v(134.37, 30.38) * mm, "end": v(137.17, 30.38) * mm});
            skLineSegment(sketch, "E295", {"start": v(137.17, 30.38) * mm, "end": v(137.17, 31.58) * mm});
            skLineSegment(sketch, "E296", {"start": v(137.17, 31.58) * mm, "end": v(138.85, 31.58) * mm});
            skLineSegment(sketch, "E297", {"start": v(138.85, 31.58) * mm, "end": v(138.85, 37.85) * mm});
            skLineSegment(sketch, "E298", {"start": v(138.85, 37.85) * mm, "end": v(139.73, 37.85) * mm});
            skLineSegment(sketch, "E299", {"start": v(139.73, 37.85) * mm, "end": v(139.73, 40.15) * mm});
            skLineSegment(sketch, "E300", {"start": v(139.73, 40.15) * mm, "end": v(138.85, 40.15) * mm});
            skLineSegment(sketch, "E301", {"start": v(138.85, 40.15) * mm, "end": v(138.85, 43.38) * mm});
            skLineSegment(sketch, "E302", {"start": v(138.85, 43.38) * mm, "end": v(132.7, 43.38) * mm});
            skLineSegment(sketch, "E303", {"start": v(132.7, 43.38) * mm, "end": v(132.7, 40.15) * mm});
            skLineSegment(sketch, "E304", {"start": v(132.7, 40.15) * mm, "end": v(130.58, 40.15) * mm});
            skLineSegment(sketch, "E305", {"start": v(130.58, 40.15) * mm, "end": v(130.58, 44.85) * mm});
            skLineSegment(sketch, "E306", {"start": v(130.58, 44.85) * mm, "end": v(117.08, 44.85) * mm});
            skLineSegment(sketch, "E307", {"start": v(-140.1, 44.85) * mm, "end": v(-126.6, 44.85) * mm});
            skLineSegment(sketch, "E308", {"start": v(-126.6, 44.85) * mm, "end": v(-126.6, 31.35) * mm});
            skLineSegment(sketch, "E309", {"start": v(-126.6, 31.35) * mm, "end": v(-140.1, 31.35) * mm});
            skLineSegment(sketch, "E310", {"start": v(-140.1, 31.35) * mm, "end": v(-140.1, 44.85) * mm});
            skLineSegment(sketch, "E311", {"start": v(-121.05, 44.85) * mm, "end": v(-107.55, 44.85) * mm});
            skLineSegment(sketch, "E312", {"start": v(-107.55, 44.85) * mm, "end": v(-107.55, 31.35) * mm});
            skLineSegment(sketch, "E313", {"start": v(-107.55, 31.35) * mm, "end": v(-121.05, 31.35) * mm});
            skLineSegment(sketch, "E314", {"start": v(-121.05, 31.35) * mm, "end": v(-121.05, 44.85) * mm});
            skLineSegment(sketch, "E315", {"start": v(-102, 44.85) * mm, "end": v(-88.5, 44.85) * mm});
            skLineSegment(sketch, "E316", {"start": v(-88.5, 44.85) * mm, "end": v(-88.5, 31.35) * mm});
            skLineSegment(sketch, "E317", {"start": v(-88.5, 31.35) * mm, "end": v(-102, 31.35) * mm});
            skLineSegment(sketch, "E318", {"start": v(-102, 31.35) * mm, "end": v(-102, 44.85) * mm});
            skLineSegment(sketch, "E319", {"start": v(-82.95, 44.85) * mm, "end": v(-69.45, 44.85) * mm});
            skLineSegment(sketch, "E320", {"start": v(-69.45, 44.85) * mm, "end": v(-69.45, 31.35) * mm});
            skLineSegment(sketch, "E321", {"start": v(-69.45, 31.35) * mm, "end": v(-82.95, 31.35) * mm});
            skLineSegment(sketch, "E322", {"start": v(-82.95, 31.35) * mm, "end": v(-82.95, 44.85) * mm});
            skLineSegment(sketch, "E323", {"start": v(-63.9, 44.85) * mm, "end": v(-50.4, 44.85) * mm});
            skLineSegment(sketch, "E324", {"start": v(-50.4, 44.85) * mm, "end": v(-50.4, 31.35) * mm});
            skLineSegment(sketch, "E325", {"start": v(-50.4, 31.35) * mm, "end": v(-63.9, 31.35) * mm});
            skLineSegment(sketch, "E326", {"start": v(-63.9, 31.35) * mm, "end": v(-63.9, 44.85) * mm});
            skLineSegment(sketch, "E327", {"start": v(-44.85, 44.85) * mm, "end": v(-31.35, 44.85) * mm});
            skLineSegment(sketch, "E328", {"start": v(-31.35, 44.85) * mm, "end": v(-31.35, 31.35) * mm});
            skLineSegment(sketch, "E329", {"start": v(-31.35, 31.35) * mm, "end": v(-44.85, 31.35) * mm});
            skLineSegment(sketch, "E330", {"start": v(-44.85, 31.35) * mm, "end": v(-44.85, 44.85) * mm});
            skLineSegment(sketch, "E331", {"start": v(-25.8, 44.85) * mm, "end": v(-12.3, 44.85) * mm});
            skLineSegment(sketch, "E332", {"start": v(-12.3, 44.85) * mm, "end": v(-12.3, 31.35) * mm});
            skLineSegment(sketch, "E333", {"start": v(-12.3, 31.35) * mm, "end": v(-25.8, 31.35) * mm});
            skLineSegment(sketch, "E334", {"start": v(-25.8, 31.35) * mm, "end": v(-25.8, 44.85) * mm});
            skLineSegment(sketch, "E335", {"start": v(-6.75, 44.85) * mm, "end": v(6.75, 44.85) * mm});
            skLineSegment(sketch, "E336", {"start": v(6.75, 44.85) * mm, "end": v(6.75, 31.35) * mm});
            skLineSegment(sketch, "E337", {"start": v(6.75, 31.35) * mm, "end": v(-6.75, 31.35) * mm});
            skLineSegment(sketch, "E338", {"start": v(-6.75, 31.35) * mm, "end": v(-6.75, 44.85) * mm});
            skLineSegment(sketch, "E339", {"start": v(12.3, 44.85) * mm, "end": v(25.8, 44.85) * mm});
            skLineSegment(sketch, "E340", {"start": v(25.8, 44.85) * mm, "end": v(25.8, 31.35) * mm});
            skLineSegment(sketch, "E341", {"start": v(25.8, 31.35) * mm, "end": v(12.3, 31.35) * mm});
            skLineSegment(sketch, "E342", {"start": v(12.3, 31.35) * mm, "end": v(12.3, 44.85) * mm});
            skLineSegment(sketch, "E343", {"start": v(31.35, 44.85) * mm, "end": v(44.85, 44.85) * mm});
            skLineSegment(sketch, "E344", {"start": v(44.85, 44.85) * mm, "end": v(44.85, 31.35) * mm});
            skLineSegment(sketch, "E345", {"start": v(44.85, 31.35) * mm, "end": v(31.35, 31.35) * mm});
            skLineSegment(sketch, "E346", {"start": v(31.35, 31.35) * mm, "end": v(31.35, 44.85) * mm});
            skLineSegment(sketch, "E347", {"start": v(50.4, 44.85) * mm, "end": v(63.9, 44.85) * mm});
            skLineSegment(sketch, "E348", {"start": v(63.9, 44.85) * mm, "end": v(63.9, 31.35) * mm});
            skLineSegment(sketch, "E349", {"start": v(63.9, 31.35) * mm, "end": v(50.4, 31.35) * mm});
            skLineSegment(sketch, "E350", {"start": v(50.4, 31.35) * mm, "end": v(50.4, 44.85) * mm});
            skLineSegment(sketch, "E351", {"start": v(69.45, 44.85) * mm, "end": v(82.95, 44.85) * mm});
            skLineSegment(sketch, "E352", {"start": v(82.95, 44.85) * mm, "end": v(82.95, 31.35) * mm});
            skLineSegment(sketch, "E353", {"start": v(82.95, 31.35) * mm, "end": v(69.45, 31.35) * mm});
            skLineSegment(sketch, "E354", {"start": v(69.45, 31.35) * mm, "end": v(69.45, 44.85) * mm});
            skLineSegment(sketch, "E355", {"start": v(88.5, 44.85) * mm, "end": v(102, 44.85) * mm});
            skLineSegment(sketch, "E356", {"start": v(102, 44.85) * mm, "end": v(102, 31.35) * mm});
            skLineSegment(sketch, "E357", {"start": v(102, 31.35) * mm, "end": v(88.5, 31.35) * mm});
            skLineSegment(sketch, "E358", {"start": v(88.5, 31.35) * mm, "end": v(88.5, 44.85) * mm});
            skLineSegment(sketch, "E359.bottom", {"start": v(6.75, -44.85) * mm, "end": v(-6.75, -44.85) * mm});
            skLineSegment(sketch, "E359.left", {"start": v(6.75, -44.85) * mm, "end": v(6.75, -40.15) * mm});
            skLineSegment(sketch, "E359.right", {"start": v(-6.75, -44.85) * mm, "end": v(-6.75, -40.15) * mm});
            skPoint(sketch, "E359.middle", {"position": v(0, -38.1) * mm});
            skLineSegment(sketch, "E360", {"start": v(-6.75, -31.35) * mm, "end": v(6.75, -31.35) * mm});
            skLineSegment(sketch, "E361", {"start": v(-18.66, -36.05) * mm, "end": v(-6.75, -36.05) * mm});
            skLineSegment(sketch, "E362", {"start": v(-18.66, -40.15) * mm, "end": v(-6.75, -40.15) * mm});
            skLineSegment(sketch, "E363.trimOffspring", {"start": v(-6.75, -36.05) * mm, "end": v(-6.75, -31.35) * mm});
            skLineSegment(sketch, "E364.trimOffspring", {"start": v(6.75, -36.05) * mm, "end": v(6.75, -31.35) * mm});
            skSolve(sketch);
        }
        {
            var Q0;
            Q0 = qSketchRegion(id + "F2", true);
            extrude(context, id + "F3", {"entities" : qUnion([Q0]), "operationType" : NewBodyOperationType.REMOVE, "endBound" : BoundingType.THROUGH_ALL, "oppositeDirection" : true, "depth" : 25 * mm});
        }
    });
